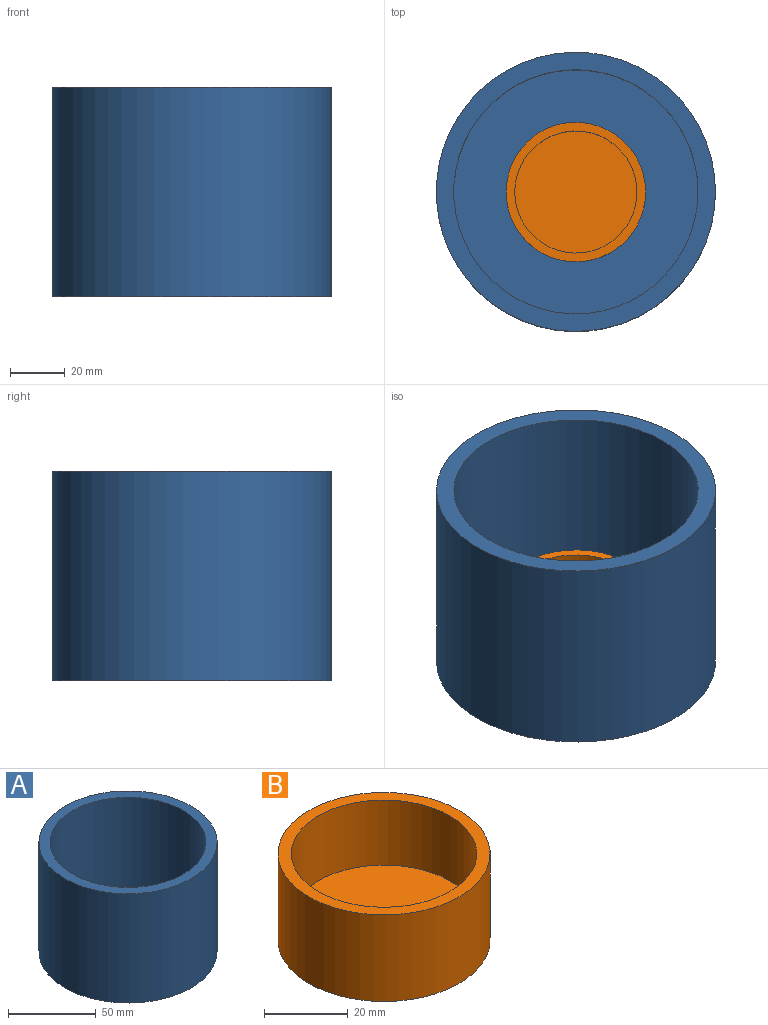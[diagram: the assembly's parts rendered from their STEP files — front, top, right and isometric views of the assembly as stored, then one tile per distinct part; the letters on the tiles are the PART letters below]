
ASSEMBLY  parts=2 mates=1
PART A: 5 faces, bbox 101.6x101.6x76.2 mm
  f0: cylinder r=44.45mm len=88.9mm, axis (0,0,-1), area 19508.2mm2, adj f2,f4
  f1: cylinder r=50.8mm len=101.6mm, axis (0,0,-1), area 24322mm2, adj f2,f3
  f2: plane 101.6x101.6mm, normal (0,0,1), area 1900.2mm2, adj f0,f1
  f3: plane 101.6x101.6mm, normal (0,0,-1), area 8107.3mm2, adj f1
  f4: plane 88.9x88.9mm, normal (0,0,1), area 6207.2mm2, adj f0
PART B: 5 faces, bbox 50.8x50.8x25.4 mm
  f0: cylinder r=22.23mm len=44.45mm, axis (0,0,-1), area 2660.2mm2, adj f2,f4
  f1: cylinder r=25.4mm len=50.8mm, axis (0,0,-1), area 4053.7mm2, adj f2,f3
  f2: plane 50.8x50.8mm, normal (0,0,1), area 475mm2, adj f0,f1
  f3: plane 50.8x50.8mm, normal (0,0,-1), area 2026.8mm2, adj f1
  f4: plane 44.45x44.45mm, normal (0,0,1), area 1551.8mm2, adj f0
PLACE A t=(75.89,-21.35,-257.91)mm
PLACE B t=(75.89,-21.35,-251.56)mm
MATE slider B.f0 <-> A.f0  axis (0,0,-1) through (75.89,-21.35,-251.56)mm
